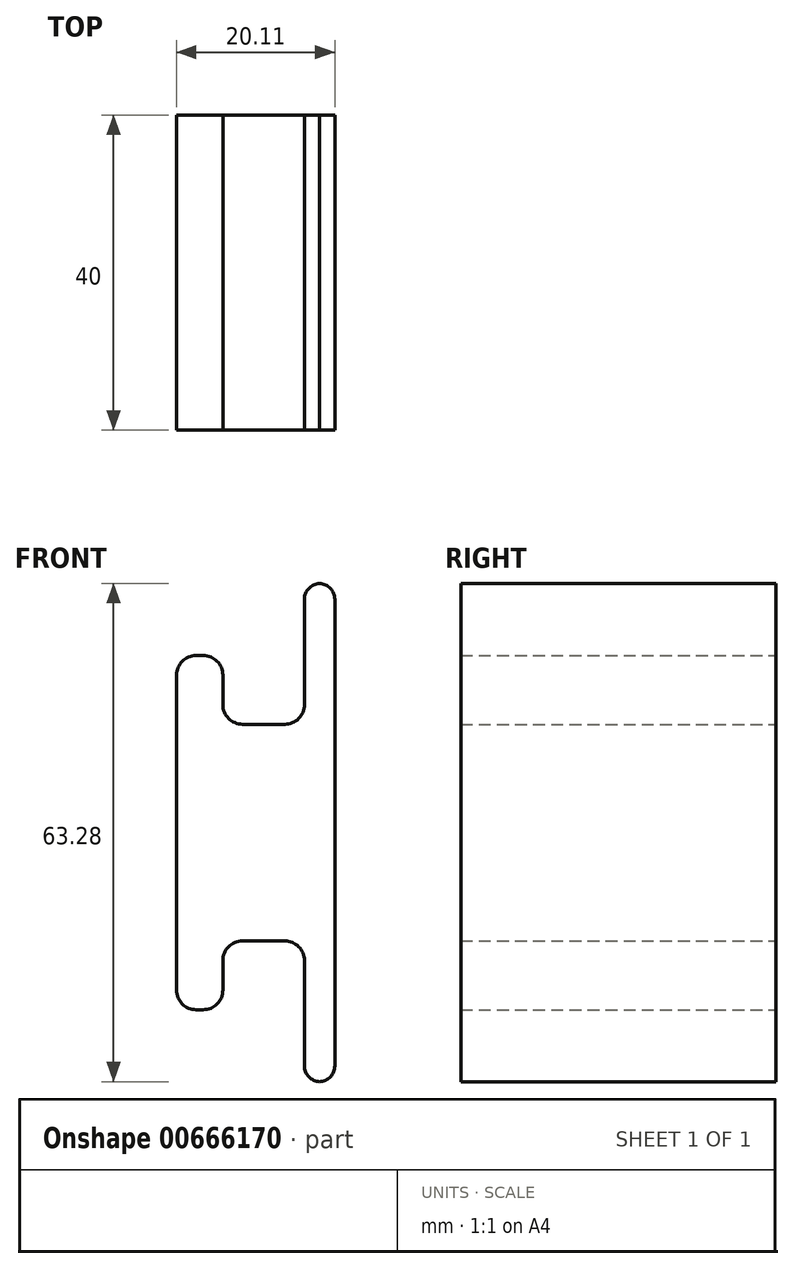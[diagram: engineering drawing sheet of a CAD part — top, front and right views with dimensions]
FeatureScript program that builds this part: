
annotation { "Feature Type Name" : "Feature", "Feature Type Description" : "" }
export const myFeature = defineFeature(function(context is Context, id is Id, definition is map)
    precondition{}
    {
        {
            var Q0;
            Q0=qCreatedBy(makeId("Front.planeOp"),FACE);
            var sketch = newSketch(context, id + "F0", { "sketchPlane" : qUnion([Q0])});
            skLineSegment(sketch, "E0", {"start": v(-23.92, 0) * mm, "end": v(-23.92, -22.5) * mm});
            skLineSegment(sketch, "E1", {"start": v(-23.92, -22.5) * mm, "end": v(-18.03, -22.5) * mm});
            skLineSegment(sketch, "E2", {"start": v(-18.03, -22.5) * mm, "end": v(-18.03, -13.76) * mm});
            skLineSegment(sketch, "E3", {"start": v(-18.03, -13.76) * mm, "end": v(-7.67, -13.76) * mm});
            skLineSegment(sketch, "E4", {"start": v(-7.67, -13.76) * mm, "end": v(-7.67, -31.64) * mm});
            skLineSegment(sketch, "E5", {"start": v(-7.67, -31.64) * mm, "end": v(-3.8, -31.64) * mm});
            skLineSegment(sketch, "E6", {"start": v(-3.8, -31.64) * mm, "end": v(-3.8, 0) * mm});
            skLineSegment(sketch, "E7.MirrorCS", {"start": v(-23.92, 0) * mm, "end": v(-23.92, 22.5) * mm});
            skLineSegment(sketch, "E8.MirrorCS", {"start": v(-23.92, 22.5) * mm, "end": v(-18.03, 22.5) * mm});
            skLineSegment(sketch, "E9.MirrorCS", {"start": v(-18.03, 13.76) * mm, "end": v(-7.67, 13.76) * mm});
            skLineSegment(sketch, "E10.MirrorCS", {"start": v(-18.03, 22.5) * mm, "end": v(-18.03, 13.76) * mm});
            skLineSegment(sketch, "E11.MirrorCS", {"start": v(-7.67, 13.76) * mm, "end": v(-7.67, 31.64) * mm});
            skLineSegment(sketch, "E12.MirrorCS", {"start": v(-7.67, 31.64) * mm, "end": v(-3.8, 31.64) * mm});
            skLineSegment(sketch, "E13.MirrorCS", {"start": v(-3.8, 31.64) * mm, "end": v(-3.8, 0) * mm});
            skPoint(sketch, "E14.orphan", {"position": v(-47.49, 0) * mm});
            skPoint(sketch, "E15.start.orphan", {"position": v(0, 40.07) * mm});
            skSolve(sketch);
        }
        {
            var Q0;
            Q0=makeQuery(id+"F0.imprint","IMPRINT",FACE,{"disambiguationData":[TD([[makeQuery(id+"F0.imprint","IMPRINT",EDGE,{"derivedFrom":sQuery(id+"F0.wireOp",EDGE,"E0")}),1.0]])]});
            extrude(context, id + "F1", {"entities" : qUnion([Q0]), "depth" : 40 * mm, "offsetDistance" : 25 * mm});
        }
        {
            var Q0;
            Q0=makeQuery(id+"F1.opExtrude","SWEPT_EDGE",EDGE,{"disambiguationData":[OSD([sQuery(id+"F0.wireOp",EDGE,"E7.MirrorCS"),sQuery(id+"F0.wireOp",EDGE,"E8.MirrorCS")])]});
            var Q1;
            Q1=makeQuery(id+"F1.opExtrude","SWEPT_EDGE",EDGE,{"disambiguationData":[OSD([sQuery(id+"F0.wireOp",EDGE,"E8.MirrorCS"),sQuery(id+"F0.wireOp",EDGE,"E10.MirrorCS")])]});
            var Q2;
            Q2=makeQuery(id+"F1.opExtrude","SWEPT_EDGE",EDGE,{"disambiguationData":[OSD([sQuery(id+"F0.wireOp",EDGE,"E0"),sQuery(id+"F0.wireOp",EDGE,"E1")])]});
            var Q3;
            Q3=makeQuery(id+"F1.opExtrude","SWEPT_EDGE",EDGE,{"disambiguationData":[OSD([sQuery(id+"F0.wireOp",EDGE,"E1"),sQuery(id+"F0.wireOp",EDGE,"E2")])]});
            var Q4;
            Q4=makeQuery(id+"F1.opExtrude","SWEPT_EDGE",EDGE,{"disambiguationData":[OSD([sQuery(id+"F0.wireOp",EDGE,"E9.MirrorCS"),sQuery(id+"F0.wireOp",EDGE,"E10.MirrorCS")])]});
            var Q5;
            Q5=makeQuery(id+"F1.opExtrude","SWEPT_EDGE",EDGE,{"disambiguationData":[OSD([sQuery(id+"F0.wireOp",EDGE,"E2"),sQuery(id+"F0.wireOp",EDGE,"E3")])]});
            var Q6;
            Q6=makeQuery(id+"F1.opExtrude","SWEPT_EDGE",EDGE,{"disambiguationData":[OSD([sQuery(id+"F0.wireOp",EDGE,"E9.MirrorCS"),sQuery(id+"F0.wireOp",EDGE,"E11.MirrorCS")])]});
            var Q7;
            Q7=makeQuery(id+"F1.opExtrude","SWEPT_EDGE",EDGE,{"disambiguationData":[OSD([sQuery(id+"F0.wireOp",EDGE,"E3"),sQuery(id+"F0.wireOp",EDGE,"E4")])]});
            fillet(context, id + "F2", {"entities" : qUnion([Q0, Q1, Q2, Q3, Q4, Q5, Q6, Q7]), "radius" : 2.5 * mm, "tangentPropagation" : true, "allowEdgeOverflow" : false});
        }
        {
            var Q0;
            Q0=makeQuery(id+"F1.opExtrude","SWEPT_EDGE",EDGE,{"disambiguationData":[OSD([sQuery(id+"F0.wireOp",EDGE,"E11.MirrorCS"),sQuery(id+"F0.wireOp",EDGE,"E12.MirrorCS")])]});
            var Q1;
            Q1=makeQuery(id+"F1.opExtrude","SWEPT_EDGE",EDGE,{"disambiguationData":[OSD([sQuery(id+"F0.wireOp",EDGE,"E12.MirrorCS"),sQuery(id+"F0.wireOp",EDGE,"E13.MirrorCS")])]});
            var Q2;
            Q2=makeQuery(id+"F1.opExtrude","SWEPT_EDGE",EDGE,{"disambiguationData":[OSD([sQuery(id+"F0.wireOp",EDGE,"E4"),sQuery(id+"F0.wireOp",EDGE,"E5")])]});
            var Q3;
            Q3=makeQuery(id+"F1.opExtrude","SWEPT_EDGE",EDGE,{"disambiguationData":[OSD([sQuery(id+"F0.wireOp",EDGE,"E5"),sQuery(id+"F0.wireOp",EDGE,"E6")])]});
            fillet(context, id + "F3", {"entities" : qUnion([Q0, Q1, Q2, Q3]), "radius" : 2 * mm, "tangentPropagation" : true, "allowEdgeOverflow" : false});
        }
    });
